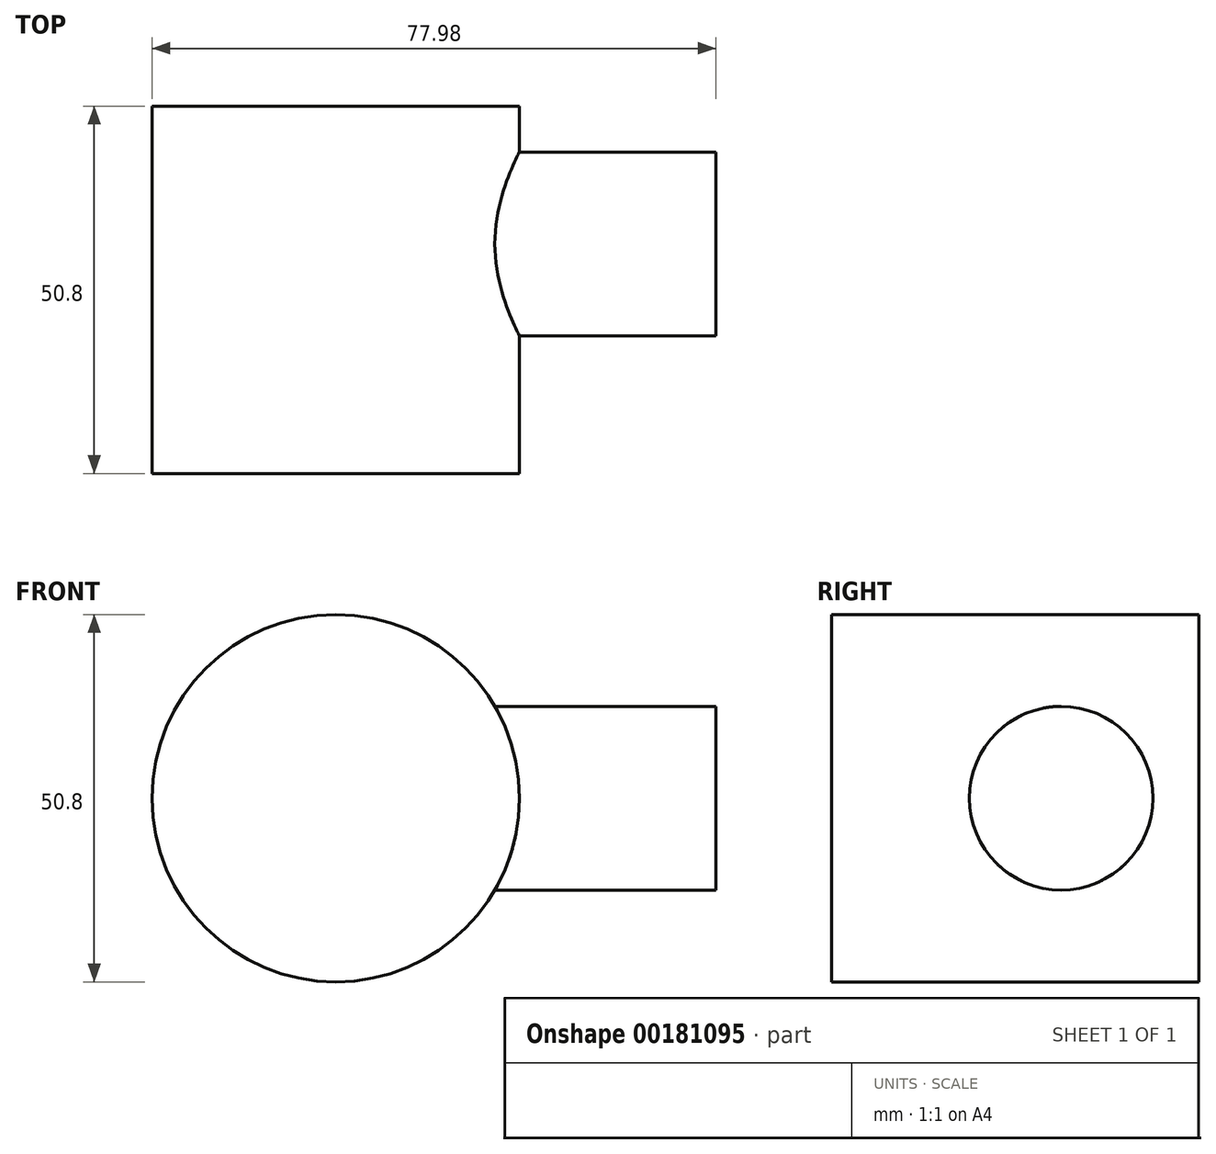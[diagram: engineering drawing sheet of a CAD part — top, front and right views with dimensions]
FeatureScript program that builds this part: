
annotation { "Feature Type Name" : "Feature", "Feature Type Description" : "" }
export const myFeature = defineFeature(function(context is Context, id is Id, definition is map)
    precondition{}
    {
        {
            var Q0;
            Q0=qCreatedBy(makeId("Front.planeOp"),FACE);
            var sketch = newSketch(context, id + "F0", { "sketchPlane" : qUnion([Q0])});
            skCircle(sketch, "E0", {"center": v(0, 0) * mm, "radius": 25.4 * mm});
            skSolve(sketch);
        }
        {
            var Q0;
            Q0=makeQuery(id+"F0.imprint","IMPRINT",FACE,{"disambiguationData":[TD([[makeQuery(id+"F0.imprint","IMPRINT",EDGE,{"derivedFrom":sQuery(id+"F0.wireOp",EDGE,"E0")}),1.0]])]});
            extrude(context, id + "F1", {"entities" : qUnion([Q0]), "depth" : 50.8 * mm});
        }
        {
            var Q0;
            Q0=qCreatedBy(makeId("Right.planeOp"),FACE);
            var sketch = newSketch(context, id + "F2", { "sketchPlane" : qUnion([Q0])});
            skCircle(sketch, "E1", {"center": v(-19.05, 0) * mm, "radius": 12.7 * mm});
            skSolve(sketch);
        }
        {
            var Q0;
            Q0 = qSketchRegion(id + "F2", true);
            extrude(context, id + "F3", {"entities" : qUnion([Q0]), "operationType" : NewBodyOperationType.ADD, "depth" : 52.58 * mm});
        }
    });
